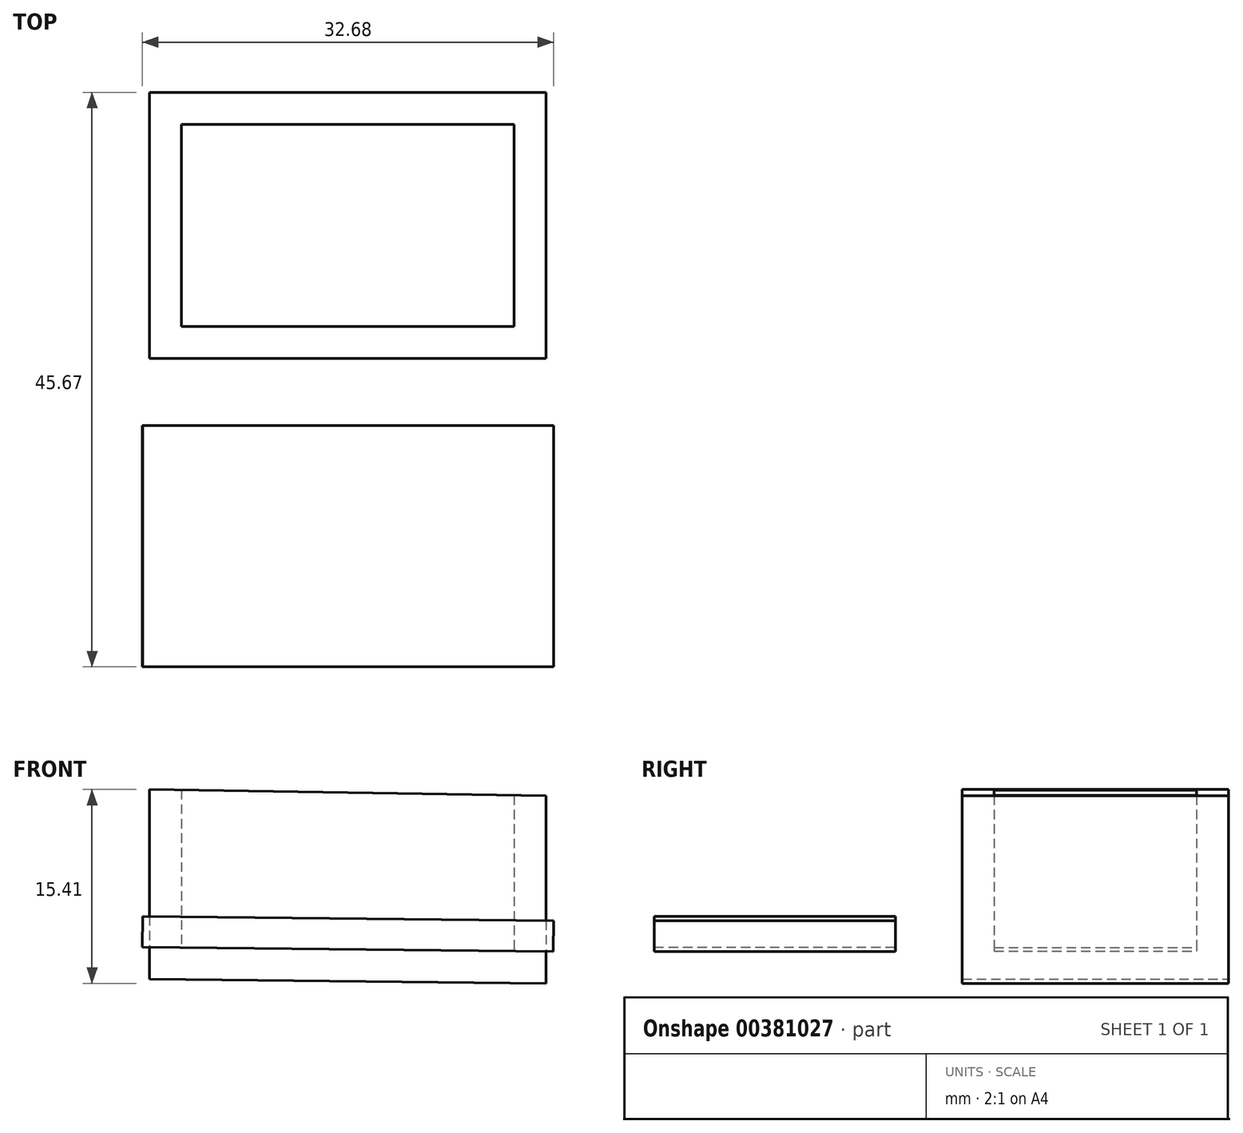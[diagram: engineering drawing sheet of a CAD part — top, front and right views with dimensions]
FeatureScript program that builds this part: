
annotation { "Feature Type Name" : "Feature", "Feature Type Description" : "" }
export const myFeature = defineFeature(function(context is Context, id is Id, definition is map)
    precondition{}
    {
        {
            var Q0;
            Q0=qCreatedBy(makeId("Front.planeOp"),FACE);
            var sketch = newSketch(context, id + "F0", { "sketchPlane" : qUnion([Q0])});
            skLineSegment(sketch, "E0", {"start": v(6.44, 35.4) * mm, "end": v(6.44, 20.5) * mm});
            skLineSegment(sketch, "E1", {"start": v(-25.07, 35.91) * mm, "end": v(-25.07, 20.83) * mm});
            skLineSegment(sketch, "E2", {"start": v(-10.16, 35.4) * mm, "end": v(-10.16, 21) * mm});
            skLineSegment(sketch, "E3", {"start": v(-25.07, 20.83) * mm, "end": v(6.44, 20.5) * mm});
            skLineSegment(sketch, "E4", {"start": v(-25.07, 35.91) * mm, "end": v(6.44, 35.4) * mm});
            skSolve(sketch);
        }
        {
            var Q0;
            Q0 = qSketchRegion(id + "F0", true);
            extrude(context, id + "F1", {"entities" : qUnion([Q0]), "depth" : 21.17 * mm});
        }
        {
            var Q0;
            Q0=makeQuery(id+"F1.opExtrude","SWEPT_FACE",FACE,{"disambiguationData":[OSD([sQuery(id+"F0.wireOp",EDGE,"E4")])]});
            shell(context, id + "F2", {"entities" : qUnion([Q0]), "thickness" : 2.54 * mm});
        }
        {
            var Q0;
            Q0=makeQuery(id+"F2.opShell","OFFSET_FACE",FACE,{"disambiguationData":[OSD([sQuery(id+"F0.wireOp",EDGE,"E3")])]});
            var sketch = newSketch(context, id + "F3", { "sketchPlane" : qUnion([Q0])});
            skLineSegment(sketch, "E5.bottom", {"start": v(6.76, -45.67) * mm, "end": v(-25.9, -45.67) * mm});
            skLineSegment(sketch, "E5.top", {"start": v(6.76, -26.49) * mm, "end": v(-25.9, -26.49) * mm});
            skLineSegment(sketch, "E5.left", {"start": v(6.76, -45.67) * mm, "end": v(6.76, -26.49) * mm});
            skLineSegment(sketch, "E5.right", {"start": v(-25.9, -45.67) * mm, "end": v(-25.9, -26.49) * mm});
            skPoint(sketch, "E5.middle", {"position": v(-9.57, -36.08) * mm});
            skPoint(sketch, "E5.middle.positionSnap0", {"position": v(-9.57, -18.63) * mm});
            skPoint(sketch, "E5.centerSnap0", {"position": v(-9.57, -18.63) * mm});
            skSolve(sketch);
        }
        {
            var Q0;
            Q0=makeQuery(id+"F3.imprint","IMPRINT",FACE,{"disambiguationData":[TD([[makeQuery(id+"F3.imprint","IMPRINT",EDGE,{"derivedFrom":sQuery(id+"F3.wireOp",EDGE,"E5.bottom")}),-1.0]])]});
            extrude(context, id + "F4", {"entities" : qUnion([Q0]), "depth" : 2.45 * mm});
        }
    });
